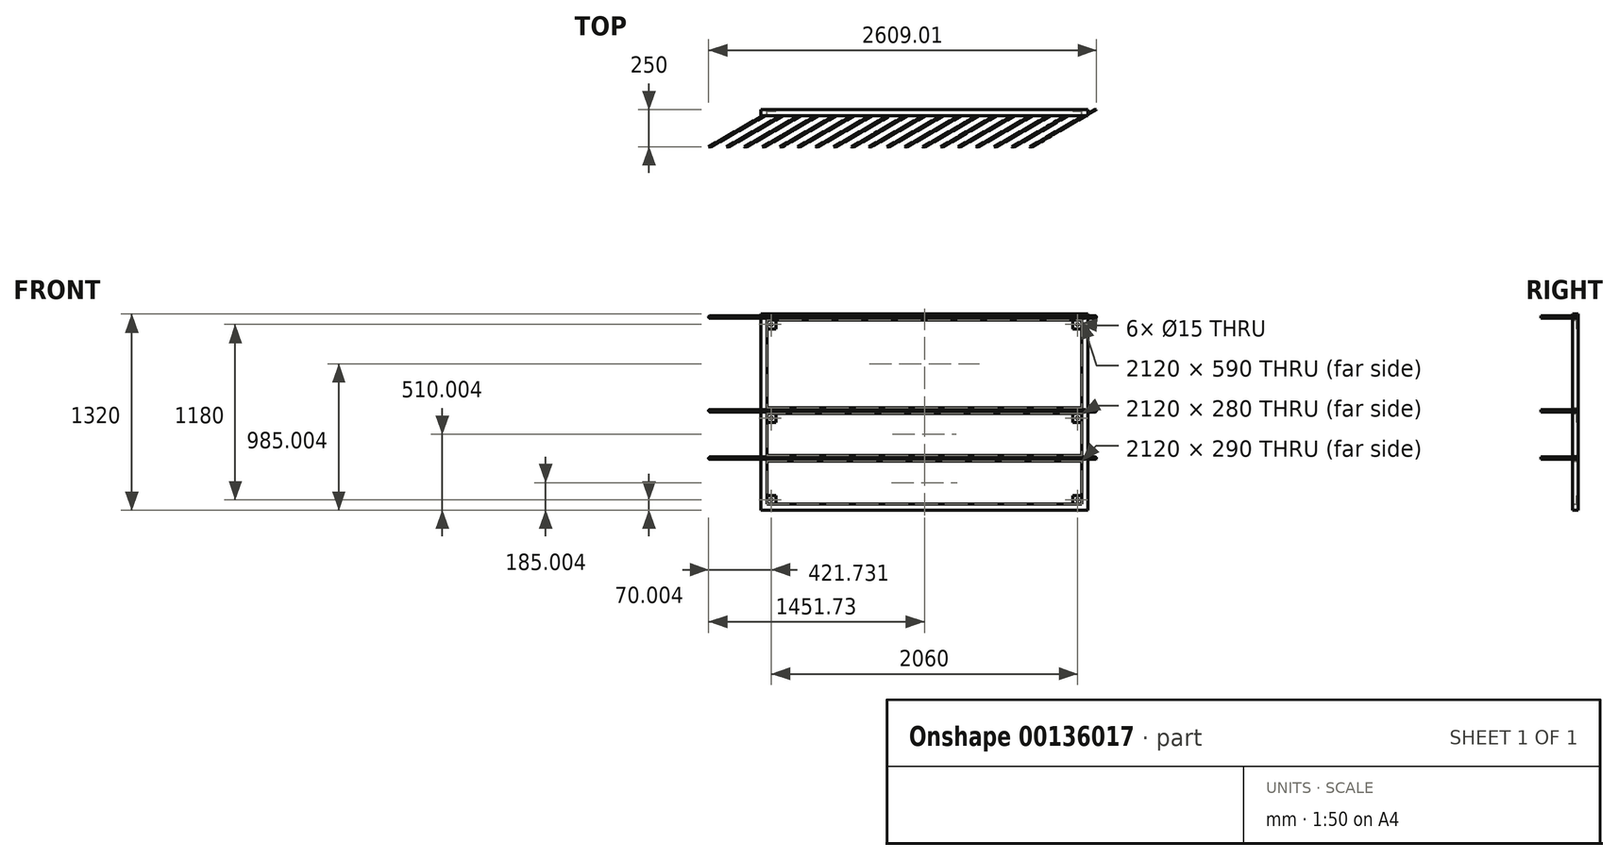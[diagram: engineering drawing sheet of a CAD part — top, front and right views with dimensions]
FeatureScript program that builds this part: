
annotation { "Feature Type Name" : "Feature", "Feature Type Description" : "" }
export const myFeature = defineFeature(function(context is Context, id is Id, definition is map)
    precondition{}
    {
        {
            var Q0;
            Q0=qCreatedBy(makeId("Front.planeOp"),FACE);
            var sketch = newSketch(context, id + "F0", { "sketchPlane" : qUnion([Q0])});
            skLineSegment(sketch, "E0.bottom", {"start": v(1099.55, 507.34) * mm, "end": v(-1100.45, 507.34) * mm});
            skLineSegment(sketch, "E0.top", {"start": v(1059.55, -482.66) * mm, "end": v(-1060.45, -482.66) * mm});
            skLineSegment(sketch, "E0.right", {"start": v(-1100.45, 507.34) * mm, "end": v(-1100.45, -812.66) * mm});
            skPoint(sketch, "E0.middle", {"position": v(-0.45, 12.34) * mm});
            skLineSegment(sketch, "E1.bottom", {"start": v(1059.55, 467.34) * mm, "end": v(-1060.45, 467.34) * mm});
            skLineSegment(sketch, "E1.top", {"start": v(1059.55, -442.66) * mm, "end": v(-1060.45, -442.66) * mm});
            skLineSegment(sketch, "E1.left", {"start": v(1059.55, 467.34) * mm, "end": v(1059.55, -122.66) * mm});
            skLineSegment(sketch, "E1.right", {"start": v(-1060.45, 467.34) * mm, "end": v(-1060.45, -122.66) * mm});
            skLineSegment(sketch, "E2", {"start": v(-1060.45, -122.66) * mm, "end": v(1059.55, -122.66) * mm});
            skLineSegment(sketch, "E3", {"start": v(-1060.45, -162.66) * mm, "end": v(1059.55, -162.66) * mm});
            skLineSegment(sketch, "E4.trimOffspring", {"start": v(-1060.45, -162.66) * mm, "end": v(-1060.45, -442.66) * mm});
            skLineSegment(sketch, "E5.trimOffspring", {"start": v(1059.55, -162.66) * mm, "end": v(1059.55, -442.66) * mm});
            skLineSegment(sketch, "E6", {"start": v(1099.55, -812.66) * mm, "end": v(-1100.45, -812.66) * mm});
            skLineSegment(sketch, "E7", {"start": v(1059.55, -482.66) * mm, "end": v(1059.55, -772.66) * mm});
            skLineSegment(sketch, "E8", {"start": v(1059.55, -772.66) * mm, "end": v(-1060.45, -772.66) * mm});
            skLineSegment(sketch, "E9", {"start": v(-1060.45, -772.66) * mm, "end": v(-1060.45, -482.66) * mm});
            skLineSegment(sketch, "E10", {"start": v(1099.55, -812.66) * mm, "end": v(1099.55, 507.34) * mm});
            skSolve(sketch);
        }
        {
            var Q0;
            Q0=makeQuery(id+"F0.imprint","IMPRINT",FACE,{"disambiguationData":[TD([[makeQuery(id+"F0.imprint","IMPRINT",EDGE,{"derivedFrom":sQuery(id+"F0.wireOp",EDGE,"E0.bottom")}),1.0]])]});
            extrude(context, id + "F1", {"entities" : qUnion([Q0]), "depth" : 40 * mm});
        }
        {
            var Q0;
            Q0=qCreatedBy(makeId("Top.planeOp"),FACE);
            var sketch = newSketch(context, id + "F2", { "sketchPlane" : qUnion([Q0])});
            skLineSegment(sketch, "E11", {"start": v(-920.45, 0) * mm, "end": v(-1353.46, -250) * mm});
            skSolve(sketch);
        }
        {
            var Q0;
            Q0=makeQuery(id+"F1.opExtrude","CAP_FACE",FACE,{"disambiguationData":[OSD([sQuery(id+"F0.wireOp",EDGE,"E0.bottom"),sQuery(id+"F0.wireOp",EDGE,"E0.top"),sQuery(id+"F0.wireOp",EDGE,"E0.right"),sQuery(id+"F0.wireOp",EDGE,"E1.bottom"),sQuery(id+"F0.wireOp",EDGE,"E1.top"),sQuery(id+"F0.wireOp",EDGE,"E1.left"),sQuery(id+"F0.wireOp",EDGE,"E1.right"),sQuery(id+"F0.wireOp",EDGE,"E2"),sQuery(id+"F0.wireOp",EDGE,"E3"),sQuery(id+"F0.wireOp",EDGE,"E4.trimOffspring"),sQuery(id+"F0.wireOp",EDGE,"E5.trimOffspring"),sQuery(id+"F0.wireOp",EDGE,"E6"),sQuery(id+"F0.wireOp",EDGE,"E7"),sQuery(id+"F0.wireOp",EDGE,"E8"),sQuery(id+"F0.wireOp",EDGE,"E9"),sQuery(id+"F0.wireOp",EDGE,"E10")])],"isStart":false});
            var sketch = newSketch(context, id + "F3", { "sketchPlane" : qUnion([Q0])});
            skCircle(sketch, "E12", {"center": v(1079.55, -142.66) * mm, "radius": 8 * mm});
            skCircle(sketch, "E13", {"center": v(1079.55, 487.34) * mm, "radius": 8 * mm});
            skCircle(sketch, "E14", {"center": v(1079.55, -462.66) * mm, "radius": 8 * mm});
            skCircle(sketch, "E15.1.0.0", {"center": v(959.55, 487.34) * mm, "radius": 8 * mm});
            skCircle(sketch, "E15.1.0.1", {"center": v(959.55, -142.66) * mm, "radius": 8 * mm});
            skCircle(sketch, "E15.1.0.2", {"center": v(959.55, -462.66) * mm, "radius": 8 * mm});
            skCircle(sketch, "E15.2.0.0", {"center": v(839.55, 487.34) * mm, "radius": 8 * mm});
            skCircle(sketch, "E15.2.0.1", {"center": v(839.55, -142.66) * mm, "radius": 8 * mm});
            skCircle(sketch, "E15.2.0.2", {"center": v(839.55, -462.66) * mm, "radius": 8 * mm});
            skCircle(sketch, "E15.3.0.0", {"center": v(719.55, 487.34) * mm, "radius": 8 * mm});
            skCircle(sketch, "E15.3.0.1", {"center": v(719.55, -142.66) * mm, "radius": 8 * mm});
            skCircle(sketch, "E15.3.0.2", {"center": v(719.55, -462.66) * mm, "radius": 8 * mm});
            skCircle(sketch, "E15.4.0.0", {"center": v(599.55, 487.34) * mm, "radius": 8 * mm});
            skCircle(sketch, "E15.4.0.1", {"center": v(599.55, -142.66) * mm, "radius": 8 * mm});
            skCircle(sketch, "E15.4.0.2", {"center": v(599.55, -462.66) * mm, "radius": 8 * mm});
            skCircle(sketch, "E15.5.0.0", {"center": v(479.55, 487.34) * mm, "radius": 8 * mm});
            skCircle(sketch, "E15.5.0.1", {"center": v(479.55, -142.66) * mm, "radius": 8 * mm});
            skCircle(sketch, "E15.5.0.2", {"center": v(479.55, -462.66) * mm, "radius": 8 * mm});
            skCircle(sketch, "E15.6.0.0", {"center": v(359.55, 487.34) * mm, "radius": 8 * mm});
            skCircle(sketch, "E15.6.0.1", {"center": v(359.55, -142.66) * mm, "radius": 8 * mm});
            skCircle(sketch, "E15.6.0.2", {"center": v(359.55, -462.66) * mm, "radius": 8 * mm});
            skCircle(sketch, "E15.7.0.0", {"center": v(239.55, 487.34) * mm, "radius": 8 * mm});
            skCircle(sketch, "E15.7.0.1", {"center": v(239.55, -142.66) * mm, "radius": 8 * mm});
            skCircle(sketch, "E15.7.0.2", {"center": v(239.55, -462.66) * mm, "radius": 8 * mm});
            skCircle(sketch, "E15.8.0.0", {"center": v(119.55, 487.34) * mm, "radius": 8 * mm});
            skCircle(sketch, "E15.8.0.1", {"center": v(119.55, -142.66) * mm, "radius": 8 * mm});
            skCircle(sketch, "E15.8.0.2", {"center": v(119.55, -462.66) * mm, "radius": 8 * mm});
            skCircle(sketch, "E15.9.0.0", {"center": v(-0.45, 487.34) * mm, "radius": 8 * mm});
            skCircle(sketch, "E15.9.0.1", {"center": v(-0.45, -142.66) * mm, "radius": 8 * mm});
            skCircle(sketch, "E15.9.0.2", {"center": v(-0.45, -462.66) * mm, "radius": 8 * mm});
            skCircle(sketch, "E15.10.0.0", {"center": v(-120.45, 487.34) * mm, "radius": 8 * mm});
            skCircle(sketch, "E15.10.0.1", {"center": v(-120.45, -142.66) * mm, "radius": 8 * mm});
            skCircle(sketch, "E15.10.0.2", {"center": v(-120.45, -462.66) * mm, "radius": 8 * mm});
            skCircle(sketch, "E15.11.0.0", {"center": v(-240.45, 487.34) * mm, "radius": 8 * mm});
            skCircle(sketch, "E15.11.0.1", {"center": v(-240.45, -142.66) * mm, "radius": 8 * mm});
            skCircle(sketch, "E15.11.0.2", {"center": v(-240.45, -462.66) * mm, "radius": 8 * mm});
            skCircle(sketch, "E15.12.0.0", {"center": v(-360.45, 487.34) * mm, "radius": 8 * mm});
            skCircle(sketch, "E15.12.0.1", {"center": v(-360.45, -142.66) * mm, "radius": 8 * mm});
            skCircle(sketch, "E15.12.0.2", {"center": v(-360.45, -462.66) * mm, "radius": 8 * mm});
            skCircle(sketch, "E15.13.0.0", {"center": v(-480.45, 487.34) * mm, "radius": 8 * mm});
            skCircle(sketch, "E15.13.0.1", {"center": v(-480.45, -142.66) * mm, "radius": 8 * mm});
            skCircle(sketch, "E15.13.0.2", {"center": v(-480.45, -462.66) * mm, "radius": 8 * mm});
            skCircle(sketch, "E15.14.0.0", {"center": v(-600.45, 487.34) * mm, "radius": 8 * mm});
            skCircle(sketch, "E15.14.0.1", {"center": v(-600.45, -142.66) * mm, "radius": 8 * mm});
            skCircle(sketch, "E15.14.0.2", {"center": v(-600.45, -462.66) * mm, "radius": 8 * mm});
            skLineSegment(sketch, "E15.direction1", {"start": v(1079.55, 487.34) * mm, "end": v(959.55, 487.34) * mm, "construction": true});
            skCircle(sketch, "E16.0.15.0", {"center": v(-720.45, 487.34) * mm, "radius": 8 * mm});
            skCircle(sketch, "E16.2.15.0", {"center": v(-720.45, -142.66) * mm, "radius": 8 * mm});
            skCircle(sketch, "E16.4.15.0", {"center": v(-720.45, -462.66) * mm, "radius": 8 * mm});
            skCircle(sketch, "E16.0.16.0", {"center": v(-840.45, 487.34) * mm, "radius": 8 * mm});
            skCircle(sketch, "E16.2.16.0", {"center": v(-840.45, -142.66) * mm, "radius": 8 * mm});
            skCircle(sketch, "E16.4.16.0", {"center": v(-840.45, -462.66) * mm, "radius": 8 * mm});
            skCircle(sketch, "E16.0.17.0", {"center": v(-960.45, 487.34) * mm, "radius": 8 * mm});
            skCircle(sketch, "E16.2.17.0", {"center": v(-960.45, -142.66) * mm, "radius": 8 * mm});
            skCircle(sketch, "E16.4.17.0", {"center": v(-960.45, -462.66) * mm, "radius": 8 * mm});
            skCircle(sketch, "E17.0.18.0", {"center": v(-1080.45, 487.34) * mm, "radius": 8 * mm});
            skCircle(sketch, "E17.2.18.0", {"center": v(-1080.45, -142.66) * mm, "radius": 8 * mm});
            skCircle(sketch, "E17.4.18.0", {"center": v(-1080.45, -462.66) * mm, "radius": 8 * mm});
            skSolve(sketch);
        }
        {
            var Q0;
            Q0 = qSketchRegion(id + "F3", true);
            var Q1;
            Q1=sQuery(id+"F2.wireOp",EDGE,"E11");
            sweep(context, id + "F4", {"operationType" : NewBodyOperationType.ADD, "profiles" : qUnion([Q0]), "path" : qUnion([Q1])});
        }
        {
            var Q0;
            Q0=makeQuery(id+"F1.opExtrude","CAP_FACE",FACE,{"disambiguationData":[OSD([sQuery(id+"F0.wireOp",EDGE,"E0.bottom"),sQuery(id+"F0.wireOp",EDGE,"E0.top"),sQuery(id+"F0.wireOp",EDGE,"E0.right"),sQuery(id+"F0.wireOp",EDGE,"E1.bottom"),sQuery(id+"F0.wireOp",EDGE,"E1.top"),sQuery(id+"F0.wireOp",EDGE,"E1.left"),sQuery(id+"F0.wireOp",EDGE,"E1.right"),sQuery(id+"F0.wireOp",EDGE,"E2"),sQuery(id+"F0.wireOp",EDGE,"E3"),sQuery(id+"F0.wireOp",EDGE,"E4.trimOffspring"),sQuery(id+"F0.wireOp",EDGE,"E5.trimOffspring"),sQuery(id+"F0.wireOp",EDGE,"E6"),sQuery(id+"F0.wireOp",EDGE,"E7"),sQuery(id+"F0.wireOp",EDGE,"E8"),sQuery(id+"F0.wireOp",EDGE,"E9"),sQuery(id+"F0.wireOp",EDGE,"E10")])],"isStart":true});
            var sketch = newSketch(context, id + "F5", { "sketchPlane" : qUnion([Q0])});
            skLineSegment(sketch, "E18.bottom", {"start": v(1000.45, 467.34) * mm, "end": v(1060.45, 467.34) * mm});
            skLineSegment(sketch, "E18.top", {"start": v(1000.45, 407.34) * mm, "end": v(1060.45, 407.34) * mm});
            skLineSegment(sketch, "E18.left", {"start": v(1000.45, 467.34) * mm, "end": v(1000.45, 407.34) * mm});
            skLineSegment(sketch, "E18.right", {"start": v(1060.45, 467.34) * mm, "end": v(1060.45, 407.34) * mm});
            skLineSegment(sketch, "E19.bottom", {"start": v(-999.55, 467.34) * mm, "end": v(-1059.55, 467.34) * mm});
            skLineSegment(sketch, "E19.top", {"start": v(-999.55, 407.34) * mm, "end": v(-1059.55, 407.34) * mm});
            skLineSegment(sketch, "E19.left", {"start": v(-999.55, 467.34) * mm, "end": v(-999.55, 407.34) * mm});
            skLineSegment(sketch, "E19.right", {"start": v(-1059.55, 467.34) * mm, "end": v(-1059.55, 407.34) * mm});
            skLineSegment(sketch, "E20.bottom", {"start": v(-999.55, -162.66) * mm, "end": v(-1059.55, -162.66) * mm});
            skLineSegment(sketch, "E20.top", {"start": v(-999.55, -222.66) * mm, "end": v(-1059.55, -222.66) * mm});
            skLineSegment(sketch, "E20.left", {"start": v(-999.55, -162.66) * mm, "end": v(-999.55, -222.66) * mm});
            skLineSegment(sketch, "E20.right", {"start": v(-1059.55, -162.66) * mm, "end": v(-1059.55, -222.66) * mm});
            skLineSegment(sketch, "E21.bottom", {"start": v(1000.45, -162.66) * mm, "end": v(1060.45, -162.66) * mm});
            skLineSegment(sketch, "E21.top", {"start": v(1000.45, -222.66) * mm, "end": v(1060.45, -222.66) * mm});
            skLineSegment(sketch, "E21.left", {"start": v(1000.45, -162.66) * mm, "end": v(1000.45, -222.66) * mm});
            skLineSegment(sketch, "E21.right", {"start": v(1060.45, -162.66) * mm, "end": v(1060.45, -222.66) * mm});
            skLineSegment(sketch, "E22.bottom", {"start": v(1000.45, -712.66) * mm, "end": v(1060.45, -712.66) * mm});
            skLineSegment(sketch, "E22.top", {"start": v(1000.45, -772.66) * mm, "end": v(1060.45, -772.66) * mm});
            skLineSegment(sketch, "E22.left", {"start": v(1000.45, -712.66) * mm, "end": v(1000.45, -772.66) * mm});
            skLineSegment(sketch, "E22.right", {"start": v(1060.45, -712.66) * mm, "end": v(1060.45, -772.66) * mm});
            skLineSegment(sketch, "E23.bottom", {"start": v(-999.55, -712.66) * mm, "end": v(-1059.55, -712.66) * mm});
            skLineSegment(sketch, "E23.top", {"start": v(-999.55, -772.66) * mm, "end": v(-1059.55, -772.66) * mm});
            skLineSegment(sketch, "E23.left", {"start": v(-999.55, -712.66) * mm, "end": v(-999.55, -772.66) * mm});
            skLineSegment(sketch, "E23.right", {"start": v(-1059.55, -712.66) * mm, "end": v(-1059.55, -772.66) * mm});
            skCircle(sketch, "E24", {"center": v(1030.45, 437.34) * mm, "radius": 7.5 * mm});
            skPoint(sketch, "E24.centerSnap0", {"position": v(1030.45, 467.34) * mm});
            skPoint(sketch, "E24.centerSnap1", {"position": v(1000.45, 437.34) * mm});
            skCircle(sketch, "E25", {"center": v(-1029.55, 437.34) * mm, "radius": 7.5 * mm});
            skPoint(sketch, "E25.centerSnap0", {"position": v(-1029.55, 467.34) * mm});
            skPoint(sketch, "E25.centerSnap1", {"position": v(-1059.55, 437.34) * mm});
            skCircle(sketch, "E26", {"center": v(-1029.55, -192.66) * mm, "radius": 7.5 * mm});
            skPoint(sketch, "E26.centerSnap0", {"position": v(-1029.55, -162.66) * mm});
            skPoint(sketch, "E26.centerSnap1", {"position": v(-1059.55, -192.66) * mm});
            skCircle(sketch, "E27", {"center": v(1030.45, -192.66) * mm, "radius": 7.5 * mm});
            skPoint(sketch, "E27.centerSnap0", {"position": v(1030.45, -162.66) * mm});
            skPoint(sketch, "E27.centerSnap1", {"position": v(1060.45, -192.66) * mm});
            skCircle(sketch, "E28", {"center": v(1030.45, -742.66) * mm, "radius": 7.5 * mm});
            skPoint(sketch, "E28.centerSnap0", {"position": v(1030.45, -772.66) * mm});
            skPoint(sketch, "E28.centerSnap1", {"position": v(1060.45, -742.66) * mm});
            skCircle(sketch, "E29", {"center": v(-1029.55, -742.66) * mm, "radius": 7.5 * mm});
            skPoint(sketch, "E29.centerSnap0", {"position": v(-1029.55, -772.66) * mm});
            skPoint(sketch, "E29.centerSnap1", {"position": v(-1059.55, -742.66) * mm});
            skSolve(sketch);
        }
        {
            var Q0;
            Q0=makeQuery(id+"F5.imprint","IMPRINT",FACE,{"disambiguationData":[TD([[makeQuery(id+"F5.imprint","IMPRINT",EDGE,{"derivedFrom":sQuery(id+"F5.wireOp",EDGE,"E18.bottom")}),1.0]])]});
            var Q1;
            Q1=makeQuery(id+"F5.imprint","IMPRINT",FACE,{"disambiguationData":[TD([[makeQuery(id+"F5.imprint","IMPRINT",EDGE,{"derivedFrom":sQuery(id+"F5.wireOp",EDGE,"E21.bottom")}),-1.0]])]});
            var Q2;
            Q2=makeQuery(id+"F5.imprint","IMPRINT",FACE,{"disambiguationData":[TD([[makeQuery(id+"F5.imprint","IMPRINT",EDGE,{"derivedFrom":sQuery(id+"F5.wireOp",EDGE,"E23.bottom")}),1.0]])]});
            var Q3;
            Q3=makeQuery(id+"F5.imprint","IMPRINT",FACE,{"disambiguationData":[TD([[makeQuery(id+"F5.imprint","IMPRINT",EDGE,{"derivedFrom":sQuery(id+"F5.wireOp",EDGE,"E20.bottom")}),-1.0]])]});
            var Q4;
            Q4=makeQuery(id+"F5.imprint","IMPRINT",FACE,{"disambiguationData":[TD([[makeQuery(id+"F5.imprint","IMPRINT",EDGE,{"derivedFrom":sQuery(id+"F5.wireOp",EDGE,"E19.bottom")}),1.0]])]});
            var Q5;
            Q5=makeQuery(id+"F5.imprint","IMPRINT",FACE,{"disambiguationData":[TD([[makeQuery(id+"F5.imprint","IMPRINT",EDGE,{"derivedFrom":sQuery(id+"F5.wireOp",EDGE,"E22.bottom")}),-1.0]])]});
            var Q6;
            Q6=makeQuery(id+"F5.imprint","IMPRINT",FACE,{"disambiguationData":[TD([[makeQuery(id+"F5.imprint","IMPRINT",EDGE,{"derivedFrom":sQuery(id+"F5.wireOp",EDGE,"E19.bottom")}),-1.0]])]});
            var Q7;
            Q7=makeQuery(id+"F5.imprint","IMPRINT",FACE,{"disambiguationData":[TD([[makeQuery(id+"F5.imprint","IMPRINT",EDGE,{"derivedFrom":sQuery(id+"F5.wireOp",EDGE,"E20.bottom")}),1.0]])]});
            var Q8;
            Q8=makeQuery(id+"F5.imprint","IMPRINT",FACE,{"disambiguationData":[TD([[makeQuery(id+"F5.imprint","IMPRINT",EDGE,{"derivedFrom":sQuery(id+"F5.wireOp",EDGE,"E21.bottom")}),1.0]])]});
            var Q9;
            Q9=makeQuery(id+"F5.imprint","IMPRINT",FACE,{"disambiguationData":[TD([[makeQuery(id+"F5.imprint","IMPRINT",EDGE,{"derivedFrom":sQuery(id+"F5.wireOp",EDGE,"E18.bottom")}),-1.0]])]});
            extrude(context, id + "F6", {"entities" : qUnion([Q0, Q1, Q2, Q3, Q4, Q5, Q6, Q7, Q8, Q9]), "operationType" : NewBodyOperationType.ADD, "oppositeDirection" : true, "depth" : 10 * mm});
        }
    });
